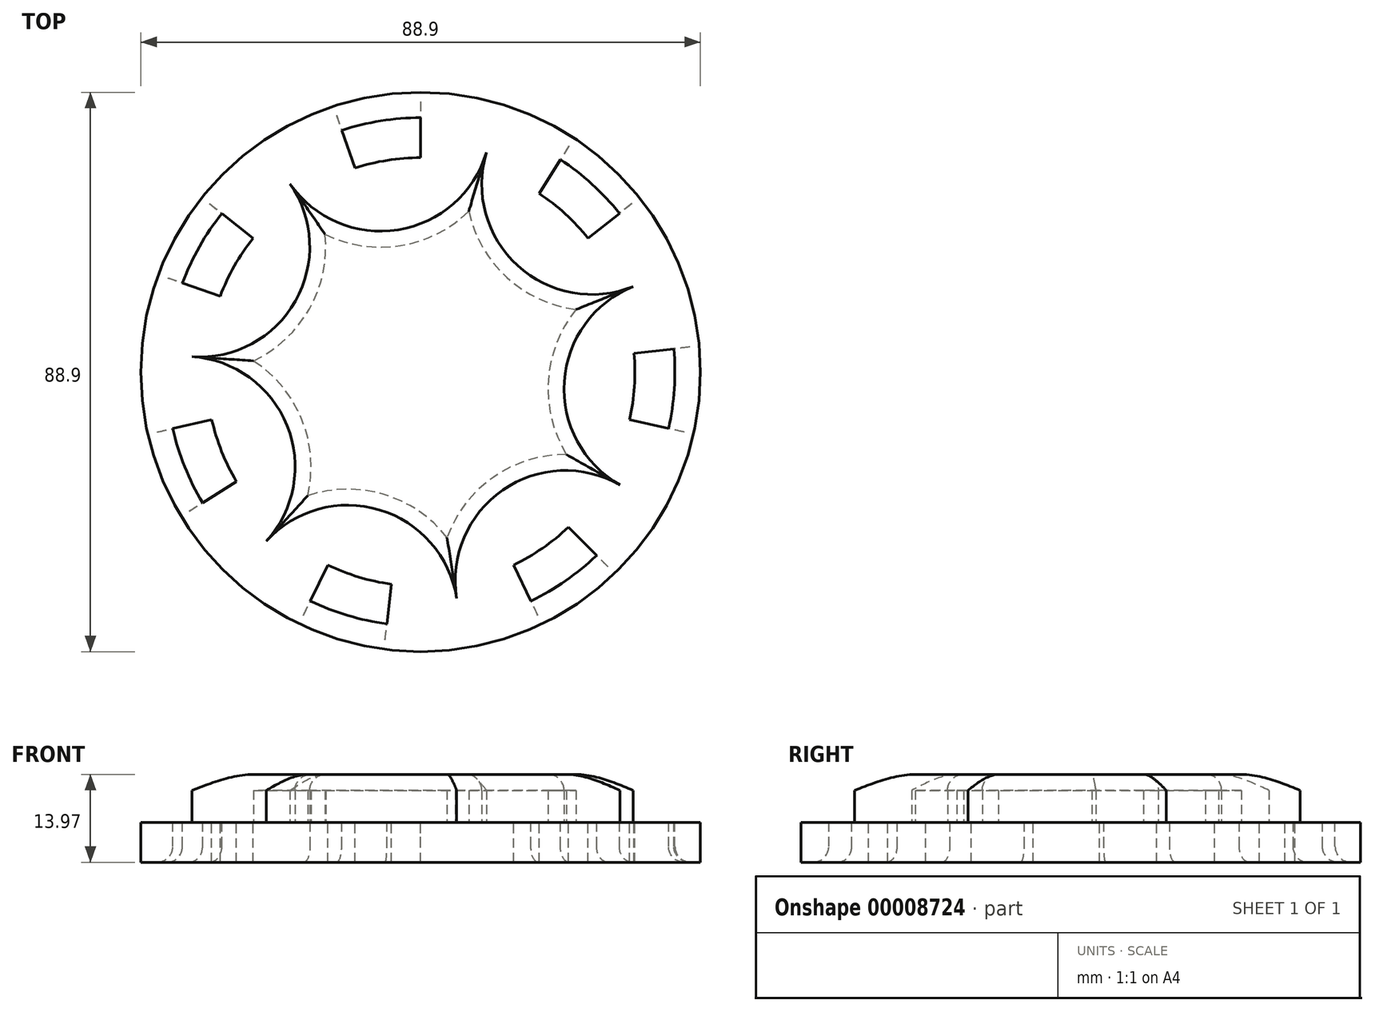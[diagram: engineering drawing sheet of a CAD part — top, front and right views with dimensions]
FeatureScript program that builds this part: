
annotation { "Feature Type Name" : "Feature", "Feature Type Description" : "" }
export const myFeature = defineFeature(function(context is Context, id is Id, definition is map)
    precondition{}
    {
        {
            var Q0;
            Q0=qCreatedBy(makeId("Top.planeOp"),FACE);
            var sketch = newSketch(context, id + "F0", { "sketchPlane" : qUnion([Q0])});
            skCircle(sketch, "E0", {"center": v(0, 0) * mm, "radius": 44.45 * mm});
            skSolve(sketch);
        }
        {
            var Q0;
            Q0=makeQuery(id+"F0.imprint","IMPRINT",FACE,{"disambiguationData":[TD([[makeQuery(id+"F0.imprint","IMPRINT",EDGE,{"derivedFrom":sQuery(id+"F0.wireOp",EDGE,"E0")}),1.0]])]});
            var sketch = newSketch(context, id + "F1", { "sketchPlane" : qUnion([Q0])});
            skArc(sketch, "E1", {"start": v(0, 40.4) * mm, "mid": v(-6.35, 39.9) * mm, "end": v(-12.54, 38.4) * mm});
            skArc(sketch, "E2.0", {"start": v(0, 34.05) * mm, "mid": v(-5.29, 33.64) * mm, "end": v(-10.45, 32.4) * mm});
            skLineSegment(sketch, "E3", {"start": v(-12.54, 38.4) * mm, "end": v(-10.45, 32.4) * mm});
            skLineSegment(sketch, "E4", {"start": v(0, 40.4) * mm, "end": v(0, 34.05) * mm});
            skSolve(sketch);
        }
        {
            var Q0;
            Q0 = qSketchRegion(id + "F0", true);
            extrude(context, id + "F2", {"entities" : qUnion([Q0]), "oppositeDirection" : true, "depth" : 6.35 * mm});
        }
        {
            var Q0;
            Q0=qCreatedBy(makeId("Front.planeOp"),FACE);
            var sketch = newSketch(context, id + "F3", { "sketchPlane" : qUnion([Q0])});
            skLineSegment(sketch, "E5", {"start": v(0, -56.34) * mm, "end": v(0, 52.87) * mm, "construction": true});
            skSolve(sketch);
        }
        {
            var Q0;
            Q0 = qSketchRegion(id + "F1", true);
            extrude(context, id + "F4", {"entities" : qUnion([Q0]), "oppositeDirection" : true, "depth" : 7.62 * mm});
        }
        {
            var Q0;
            Q0=makeQuery(id+"F4.opExtrude","SWEPT_BODY",BODY,{"disambiguationData":[OSD([sQuery(id+"F1.wireOp",EDGE,"E1"),sQuery(id+"F1.wireOp",EDGE,"E2.0"),sQuery(id+"F1.wireOp",EDGE,"E3"),sQuery(id+"F1.wireOp",EDGE,"E4")])]});
            var Q1;
            Q1=sQuery(id+"F3.wireOp",EDGE,"E5");
            circularPattern(context, id + "F5", {"entities" : qUnion([Q0]), "axis" : qUnion([Q1]), "angle" : 51.43 * degree, "instanceCount" : 7});
        }
        {
            var Q0;
            Q0=makeQuery(id+"F5.opPattern","COPY",BODY,{"derivedFrom":makeQuery(id+"F4.opExtrude","SWEPT_BODY",BODY,{"disambiguationData":[OSD([sQuery(id+"F1.wireOp",EDGE,"E1"),sQuery(id+"F1.wireOp",EDGE,"E2.0"),sQuery(id+"F1.wireOp",EDGE,"E3"),sQuery(id+"F1.wireOp",EDGE,"E4")])]}),"instanceName":"1"});
            var Q1;
            Q1=makeQuery(id+"F4.opExtrude","SWEPT_BODY",BODY,{"disambiguationData":[OSD([sQuery(id+"F1.wireOp",EDGE,"E1"),sQuery(id+"F1.wireOp",EDGE,"E2.0"),sQuery(id+"F1.wireOp",EDGE,"E3"),sQuery(id+"F1.wireOp",EDGE,"E4")])]});
            var Q2;
            Q2=makeQuery(id+"F5.opPattern","COPY",BODY,{"derivedFrom":makeQuery(id+"F4.opExtrude","SWEPT_BODY",BODY,{"disambiguationData":[OSD([sQuery(id+"F1.wireOp",EDGE,"E1"),sQuery(id+"F1.wireOp",EDGE,"E2.0"),sQuery(id+"F1.wireOp",EDGE,"E3"),sQuery(id+"F1.wireOp",EDGE,"E4")])]}),"instanceName":"2"});
            var Q3;
            Q3=makeQuery(id+"F5.opPattern","COPY",BODY,{"derivedFrom":makeQuery(id+"F4.opExtrude","SWEPT_BODY",BODY,{"disambiguationData":[OSD([sQuery(id+"F1.wireOp",EDGE,"E1"),sQuery(id+"F1.wireOp",EDGE,"E2.0"),sQuery(id+"F1.wireOp",EDGE,"E3"),sQuery(id+"F1.wireOp",EDGE,"E4")])]}),"instanceName":"3"});
            var Q4;
            Q4=makeQuery(id+"F5.opPattern","COPY",BODY,{"derivedFrom":makeQuery(id+"F4.opExtrude","SWEPT_BODY",BODY,{"disambiguationData":[OSD([sQuery(id+"F1.wireOp",EDGE,"E1"),sQuery(id+"F1.wireOp",EDGE,"E2.0"),sQuery(id+"F1.wireOp",EDGE,"E3"),sQuery(id+"F1.wireOp",EDGE,"E4")])]}),"instanceName":"4"});
            var Q5;
            Q5=makeQuery(id+"F5.opPattern","COPY",BODY,{"derivedFrom":makeQuery(id+"F4.opExtrude","SWEPT_BODY",BODY,{"disambiguationData":[OSD([sQuery(id+"F1.wireOp",EDGE,"E1"),sQuery(id+"F1.wireOp",EDGE,"E2.0"),sQuery(id+"F1.wireOp",EDGE,"E3"),sQuery(id+"F1.wireOp",EDGE,"E4")])]}),"instanceName":"5"});
            var Q6;
            Q6=makeQuery(id+"F5.opPattern","COPY",BODY,{"derivedFrom":makeQuery(id+"F4.opExtrude","SWEPT_BODY",BODY,{"disambiguationData":[OSD([sQuery(id+"F1.wireOp",EDGE,"E1"),sQuery(id+"F1.wireOp",EDGE,"E2.0"),sQuery(id+"F1.wireOp",EDGE,"E3"),sQuery(id+"F1.wireOp",EDGE,"E4")])]}),"instanceName":"6"});
            var Q7;
            Q7=makeQuery(id+"F2.opExtrude","SWEPT_BODY",BODY,{"disambiguationData":[OSD([sQuery(id+"F0.wireOp",EDGE,"E0")])]});
            booleanBodies(context, id + "F6", {"operationType" : BooleanOperationType.SUBTRACTION, "tools" : qUnion([Q0, Q1, Q2, Q3, Q4, Q5, Q6]), "targets" : qUnion([Q7])});
        }
        {
            var Q0;
            Q0=makeQuery(id+"F1.imprint","IMPRINT",FACE,{"disambiguationData":[TD([[makeQuery(id+"F1.imprint","IMPRINT",EDGE,{"derivedFrom":sQuery(id+"F1.wireOp",EDGE,"E1")}),-1.0]])]});
            var sketch = newSketch(context, id + "F7", { "sketchPlane" : qUnion([Q0])});
            skLineSegment(sketch, "E6", {"start": v(40.31, -2.69) * mm, "end": v(23.03, -33.2) * mm, "construction": true});
            skLineSegment(sketch, "E7", {"start": v(23.03, -33.2) * mm, "end": v(-11.59, -38.7) * mm, "construction": true});
            skLineSegment(sketch, "E8", {"start": v(-11.59, -38.7) * mm, "end": v(-37.48, -15.07) * mm, "construction": true});
            skLineSegment(sketch, "E9", {"start": v(-35.15, 19.91) * mm, "end": v(-6.35, 39.9) * mm, "construction": true});
            skLineSegment(sketch, "E10", {"start": v(-6.35, 39.9) * mm, "end": v(27.23, 29.84) * mm, "construction": true});
            skLineSegment(sketch, "E11", {"start": v(27.23, 29.84) * mm, "end": v(40.31, -2.69) * mm, "construction": true});
            skLineSegment(sketch, "E12", {"start": v(-37.48, -15.07) * mm, "end": v(-35.15, 19.91) * mm, "construction": true});
            skLineSegment(sketch, "E13", {"start": v(0, 0) * mm, "end": v(33.77, 13.58) * mm, "construction": true});
            skLineSegment(sketch, "E14", {"start": v(0, 0) * mm, "end": v(31.67, -17.94) * mm, "construction": true});
            skLineSegment(sketch, "E15", {"start": v(0, 0) * mm, "end": v(5.72, -35.95) * mm, "construction": true});
            skLineSegment(sketch, "E16", {"start": v(0, 0) * mm, "end": v(-24.54, -26.89) * mm, "construction": true});
            skLineSegment(sketch, "E17", {"start": v(0, 0) * mm, "end": v(-36.32, 2.42) * mm, "construction": true});
            skLineSegment(sketch, "E18", {"start": v(0, 0) * mm, "end": v(-20.75, 29.9) * mm, "construction": true});
            skLineSegment(sketch, "E19", {"start": v(0, 0) * mm, "end": v(10.44, 34.87) * mm, "construction": true});
            skArc(sketch, "E20", {"start": v(33.77, 13.58) * mm, "mid": v(22.82, -1.52) * mm, "end": v(31.67, -17.94) * mm});
            skArc(sketch, "E21", {"start": v(31.67, -17.94) * mm, "mid": v(13.04, -18.8) * mm, "end": v(5.72, -35.95) * mm});
            skArc(sketch, "E22", {"start": v(5.72, -35.95) * mm, "mid": v(-6.56, -21.9) * mm, "end": v(-24.54, -26.89) * mm});
            skArc(sketch, "E23", {"start": v(-24.54, -26.89) * mm, "mid": v(-21.22, -8.53) * mm, "end": v(-36.32, 2.42) * mm});
            skArc(sketch, "E24", {"start": v(-36.32, 2.42) * mm, "mid": v(-19.9, 11.27) * mm, "end": v(-20.75, 29.9) * mm});
            skArc(sketch, "E25", {"start": v(-20.75, 29.9) * mm, "mid": v(-3.6, 22.59) * mm, "end": v(10.44, 34.87) * mm});
            skArc(sketch, "E26", {"start": v(10.44, 34.87) * mm, "mid": v(15.42, 16.9) * mm, "end": v(33.77, 13.58) * mm});
            skSolve(sketch);
        }
        {
            var Q0;
            Q0=makeQuery(id+"F6.opBoolean","COPY",EDGE,{"derivedFrom":makeQuery(id+"F5.opPattern","COPY",EDGE,{"derivedFrom":makeQuery(id+"F4.opExtrude","CAP_EDGE",EDGE,{"disambiguationData":[OSD([sQuery(id+"F1.wireOp",EDGE,"E1")])],"isStart":true}),"instanceName":"6"})});
            var Q1;
            Q1=makeQuery(id+"F6.opBoolean","COPY",EDGE,{"derivedFrom":makeQuery(id+"F5.opPattern","COPY",EDGE,{"derivedFrom":makeQuery(id+"F4.opExtrude","CAP_EDGE",EDGE,{"disambiguationData":[OSD([sQuery(id+"F1.wireOp",EDGE,"E1")])],"isStart":true}),"instanceName":"5"})});
            var Q2;
            Q2=makeQuery(id+"F6.opBoolean","COPY",EDGE,{"derivedFrom":makeQuery(id+"F5.opPattern","COPY",EDGE,{"derivedFrom":makeQuery(id+"F4.opExtrude","CAP_EDGE",EDGE,{"disambiguationData":[OSD([sQuery(id+"F1.wireOp",EDGE,"E1")])],"isStart":true}),"instanceName":"4"})});
            var Q3;
            Q3=makeQuery(id+"F6.opBoolean","COPY",EDGE,{"derivedFrom":makeQuery(id+"F5.opPattern","COPY",EDGE,{"derivedFrom":makeQuery(id+"F4.opExtrude","CAP_EDGE",EDGE,{"disambiguationData":[OSD([sQuery(id+"F1.wireOp",EDGE,"E1")])],"isStart":true}),"instanceName":"3"})});
            var Q4;
            Q4=makeQuery(id+"F6.opBoolean","COPY",EDGE,{"derivedFrom":makeQuery(id+"F5.opPattern","COPY",EDGE,{"derivedFrom":makeQuery(id+"F4.opExtrude","CAP_EDGE",EDGE,{"disambiguationData":[OSD([sQuery(id+"F1.wireOp",EDGE,"E1")])],"isStart":true}),"instanceName":"2"})});
            var Q5;
            Q5=makeQuery(id+"F6.opBoolean","COPY",EDGE,{"derivedFrom":makeQuery(id+"F5.opPattern","COPY",EDGE,{"derivedFrom":makeQuery(id+"F4.opExtrude","CAP_EDGE",EDGE,{"disambiguationData":[OSD([sQuery(id+"F1.wireOp",EDGE,"E1")])],"isStart":true}),"instanceName":"1"})});
            var Q6;
            Q6=makeQuery(id+"F6.opBoolean","COPY",EDGE,{"derivedFrom":makeQuery(id+"F4.opExtrude","CAP_EDGE",EDGE,{"disambiguationData":[OSD([sQuery(id+"F1.wireOp",EDGE,"E1")])],"isStart":true})});
            var Q7;
            Q7=makeQuery(id+"F6.opBoolean","INTERSECT",EDGE,{"derivedFrom":[makeQuery(id+"F2.opExtrude","CAP_FACE",FACE,{"disambiguationData":[OSD([sQuery(id+"F0.wireOp",EDGE,"E0")])],"isStart":false}),makeQuery(id+"F5.opPattern","COPY",FACE,{"derivedFrom":makeQuery(id+"F4.opExtrude","SWEPT_FACE",FACE,{"disambiguationData":[OSD([sQuery(id+"F1.wireOp",EDGE,"E1")])]}),"instanceName":"2"})]});
            var Q8;
            Q8=makeQuery(id+"F6.opBoolean","INTERSECT",EDGE,{"derivedFrom":[makeQuery(id+"F2.opExtrude","CAP_FACE",FACE,{"disambiguationData":[OSD([sQuery(id+"F0.wireOp",EDGE,"E0")])],"isStart":false}),makeQuery(id+"F5.opPattern","COPY",FACE,{"derivedFrom":makeQuery(id+"F4.opExtrude","SWEPT_FACE",FACE,{"disambiguationData":[OSD([sQuery(id+"F1.wireOp",EDGE,"E1")])]}),"instanceName":"3"})]});
            var Q9;
            Q9=makeQuery(id+"F6.opBoolean","INTERSECT",EDGE,{"derivedFrom":[makeQuery(id+"F2.opExtrude","CAP_FACE",FACE,{"disambiguationData":[OSD([sQuery(id+"F0.wireOp",EDGE,"E0")])],"isStart":false}),makeQuery(id+"F5.opPattern","COPY",FACE,{"derivedFrom":makeQuery(id+"F4.opExtrude","SWEPT_FACE",FACE,{"disambiguationData":[OSD([sQuery(id+"F1.wireOp",EDGE,"E1")])]}),"instanceName":"4"})]});
            var Q10;
            Q10=makeQuery(id+"F6.opBoolean","INTERSECT",EDGE,{"derivedFrom":[makeQuery(id+"F2.opExtrude","CAP_FACE",FACE,{"disambiguationData":[OSD([sQuery(id+"F0.wireOp",EDGE,"E0")])],"isStart":false}),makeQuery(id+"F5.opPattern","COPY",FACE,{"derivedFrom":makeQuery(id+"F4.opExtrude","SWEPT_FACE",FACE,{"disambiguationData":[OSD([sQuery(id+"F1.wireOp",EDGE,"E1")])]}),"instanceName":"5"})]});
            var Q11;
            Q11=makeQuery(id+"F6.opBoolean","INTERSECT",EDGE,{"derivedFrom":[makeQuery(id+"F2.opExtrude","CAP_FACE",FACE,{"disambiguationData":[OSD([sQuery(id+"F0.wireOp",EDGE,"E0")])],"isStart":false}),makeQuery(id+"F5.opPattern","COPY",FACE,{"derivedFrom":makeQuery(id+"F4.opExtrude","SWEPT_FACE",FACE,{"disambiguationData":[OSD([sQuery(id+"F1.wireOp",EDGE,"E1")])]}),"instanceName":"6"})]});
            var Q12;
            Q12=makeQuery(id+"F6.opBoolean","INTERSECT",EDGE,{"derivedFrom":[makeQuery(id+"F2.opExtrude","CAP_FACE",FACE,{"disambiguationData":[OSD([sQuery(id+"F0.wireOp",EDGE,"E0")])],"isStart":false}),makeQuery(id+"F4.opExtrude","SWEPT_FACE",FACE,{"disambiguationData":[OSD([sQuery(id+"F1.wireOp",EDGE,"E1")])]})]});
            var Q13;
            Q13=makeQuery(id+"F6.opBoolean","INTERSECT",EDGE,{"derivedFrom":[makeQuery(id+"F2.opExtrude","CAP_FACE",FACE,{"disambiguationData":[OSD([sQuery(id+"F0.wireOp",EDGE,"E0")])],"isStart":false}),makeQuery(id+"F5.opPattern","COPY",FACE,{"derivedFrom":makeQuery(id+"F4.opExtrude","SWEPT_FACE",FACE,{"disambiguationData":[OSD([sQuery(id+"F1.wireOp",EDGE,"E1")])]}),"instanceName":"1"})]});
            fillet(context, id + "F8", {"entities" : qUnion([Q0, Q1, Q2, Q3, Q4, Q5, Q6, Q7, Q8, Q9, Q10, Q11, Q12, Q13]), "radius" : 2.54 * mm, "tangentPropagation" : true, "allowEdgeOverflow" : false});
        }
        {
            var Q0;
            Q0=makeQuery(id+"F7.imprint","IMPRINT",FACE,{"disambiguationData":[TD([[makeQuery(id+"F7.imprint","IMPRINT",EDGE,{"derivedFrom":sQuery(id+"F7.wireOp",EDGE,"E20")}),-1.0]])]});
            extrude(context, id + "F9", {"entities" : qUnion([Q0]), "depth" : 7.62 * mm});
        }
        {
            var Q0;
            Q0=makeQuery(id+"F9.opExtrude","CAP_EDGE",EDGE,{"disambiguationData":[OSD([sQuery(id+"F7.wireOp",EDGE,"E22")])],"isStart":false});
            var Q1;
            Q1=makeQuery(id+"F9.opExtrude","CAP_EDGE",EDGE,{"disambiguationData":[OSD([sQuery(id+"F7.wireOp",EDGE,"E21")])],"isStart":false});
            var Q2;
            Q2=makeQuery(id+"F9.opExtrude","CAP_EDGE",EDGE,{"disambiguationData":[OSD([sQuery(id+"F7.wireOp",EDGE,"E20")])],"isStart":false});
            var Q3;
            Q3=makeQuery(id+"F9.opExtrude","CAP_EDGE",EDGE,{"disambiguationData":[OSD([sQuery(id+"F7.wireOp",EDGE,"E26")])],"isStart":false});
            var Q4;
            Q4=makeQuery(id+"F9.opExtrude","CAP_EDGE",EDGE,{"disambiguationData":[OSD([sQuery(id+"F7.wireOp",EDGE,"E25")])],"isStart":false});
            var Q5;
            Q5=makeQuery(id+"F9.opExtrude","CAP_EDGE",EDGE,{"disambiguationData":[OSD([sQuery(id+"F7.wireOp",EDGE,"E24")])],"isStart":false});
            var Q6;
            Q6=makeQuery(id+"F9.opExtrude","CAP_EDGE",EDGE,{"disambiguationData":[OSD([sQuery(id+"F7.wireOp",EDGE,"E23")])],"isStart":false});
            fillet(context, id + "F10", {"entities" : qUnion([Q0, Q1, Q2, Q3, Q4, Q5, Q6]), "radius" : 2.54 * mm, "tangentPropagation" : true, "allowEdgeOverflow" : false});
        }
        {
            var Q0;
            Q0=makeQuery(id+"F9.opExtrude","CAP_FACE",FACE,{"disambiguationData":[OSD([sQuery(id+"F7.wireOp",EDGE,"E20"),sQuery(id+"F7.wireOp",EDGE,"E21"),sQuery(id+"F7.wireOp",EDGE,"E22"),sQuery(id+"F7.wireOp",EDGE,"E23"),sQuery(id+"F7.wireOp",EDGE,"E24"),sQuery(id+"F7.wireOp",EDGE,"E25"),sQuery(id+"F7.wireOp",EDGE,"E26")])],"isStart":true});
            shell(context, id + "F11", {"entities" : qUnion([Q0]), "thickness" : 2.54 * mm});
        }
    });
